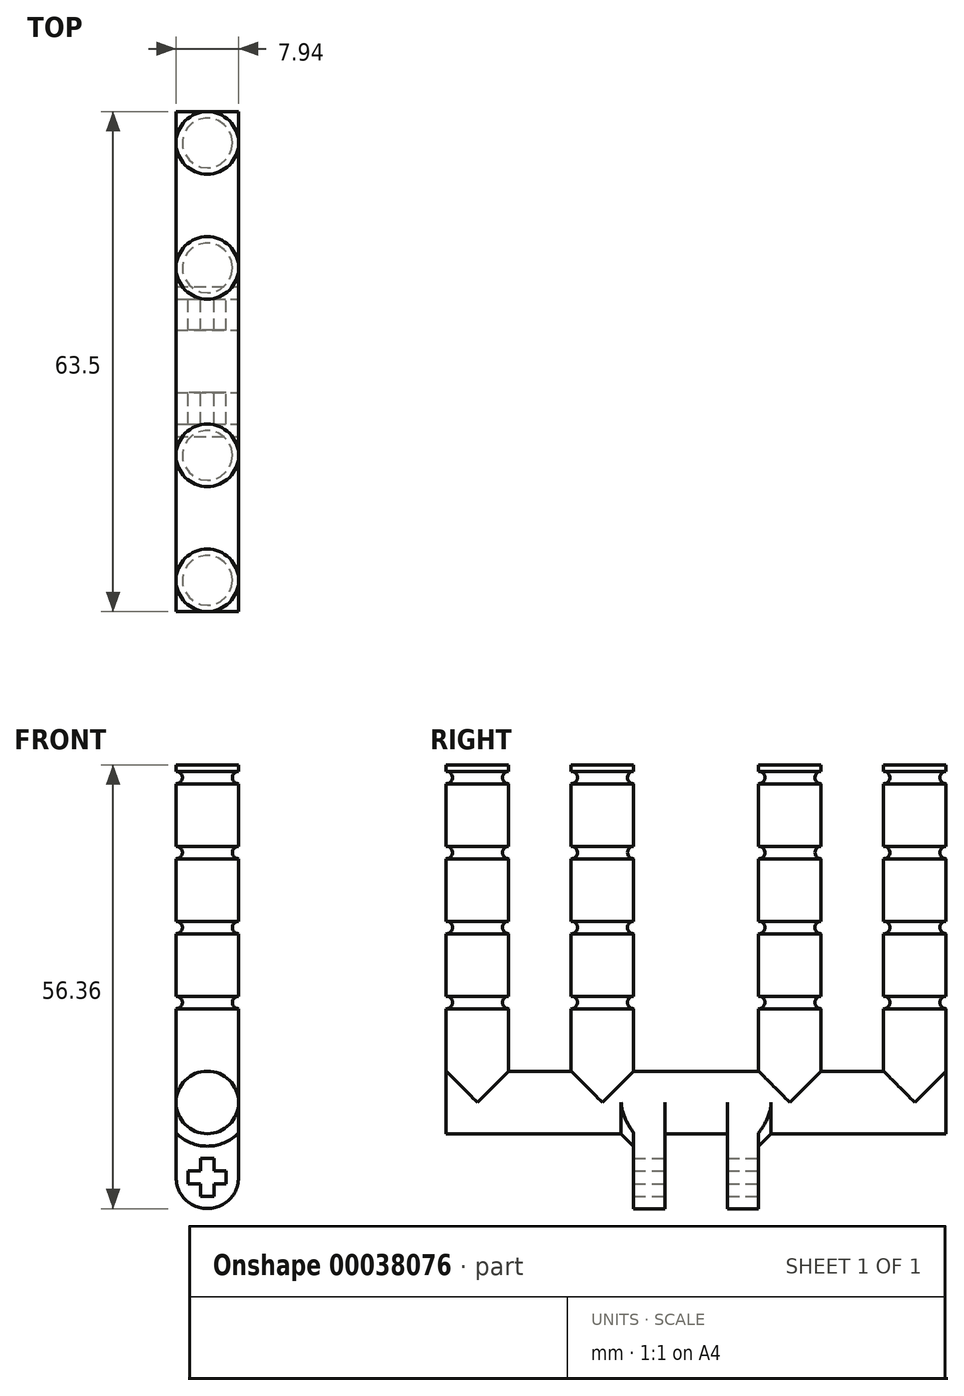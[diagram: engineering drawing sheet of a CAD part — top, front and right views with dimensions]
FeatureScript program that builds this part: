
annotation { "Feature Type Name" : "Feature", "Feature Type Description" : "" }
export const myFeature = defineFeature(function(context is Context, id is Id, definition is map)
    precondition{}
    {
        {
            var Q0;
            Q0=qCreatedBy(makeId("Top.planeOp"),FACE);
            var sketch = newSketch(context, id + "F0", { "sketchPlane" : qUnion([Q0])});
            skLineSegment(sketch, "E0.rect.bottom", {"start": v(3.97, -31.75) * mm, "end": v(-3.97, -31.75) * mm});
            skLineSegment(sketch, "E0.rect.top", {"start": v(3.97, 31.75) * mm, "end": v(-3.97, 31.75) * mm});
            skLineSegment(sketch, "E0.rect.left", {"start": v(3.97, -31.75) * mm, "end": v(3.97, 31.75) * mm});
            skLineSegment(sketch, "E0.rect.right", {"start": v(-3.97, -31.75) * mm, "end": v(-3.97, 31.75) * mm});
            skPoint(sketch, "E0.rect.middle", {"position": v(0, 0) * mm});
            skSolve(sketch);
        }
        {
            var Q0;
            Q0=qSketchRegion(id+"F0",true);
            extrude(context, id + "F1", {"entities" : qUnion([Q0]), "depth" : 7.94 * mm});
        }
        {
            var Q0;
            Q0=makeQuery(id+"F1.opExtrude","CAP_FACE",FACE,{"disambiguationData":[OSD([sQuery(id+"F0.wireOp",EDGE,"E0.rect.bottom"),sQuery(id+"F0.wireOp",EDGE,"E0.rect.top"),sQuery(id+"F0.wireOp",EDGE,"E0.rect.left"),sQuery(id+"F0.wireOp",EDGE,"E0.rect.right")])],"isStart":false});
            var sketch = newSketch(context, id + "F2", { "sketchPlane" : qUnion([Q0])});
            skLineSegment(sketch, "E1", {"start": v(0, 31.75) * mm, "end": v(0, 27.78) * mm, "construction": true});
            skLineSegment(sketch, "E2", {"start": v(0, 27.78) * mm, "end": v(0, 11.9) * mm, "construction": true});
            skLineSegment(sketch, "E3", {"start": v(0, -11.9) * mm, "end": v(0, -27.78) * mm, "construction": true});
            skLineSegment(sketch, "E4", {"start": v(0, -27.78) * mm, "end": v(0, -31.75) * mm, "construction": true});
            skCircle(sketch, "E5", {"center": v(0, 27.78) * mm, "radius": 3.97 * mm});
            skCircle(sketch, "E6", {"center": v(0, -27.78) * mm, "radius": 3.97 * mm});
            skCircle(sketch, "E7", {"center": v(0, -11.9) * mm, "radius": 3.97 * mm});
            skCircle(sketch, "E8", {"center": v(0, 11.9) * mm, "radius": 3.97 * mm});
            skSolve(sketch);
        }
        {
            var Q0;
            Q0=qSketchRegion(id+"F2",true);
            extrude(context, id + "F3", {"entities" : qUnion([Q0]), "operationType" : NewBodyOperationType.ADD, "depth" : 152.4 * mm});
        }
        {
            var Q0;
            Q0=makeQuery(id+"F1.opExtrude","CAP_FACE",FACE,{"disambiguationData":[OSD([sQuery(id+"F0.wireOp",EDGE,"E0.rect.bottom"),sQuery(id+"F0.wireOp",EDGE,"E0.rect.top"),sQuery(id+"F0.wireOp",EDGE,"E0.rect.left"),sQuery(id+"F0.wireOp",EDGE,"E0.rect.right")])],"isStart":true});
            var sketch = newSketch(context, id + "F4", { "sketchPlane" : qUnion([Q0])});
            skLineSegment(sketch, "E9", {"start": v(3.97, 0) * mm, "end": v(0, 0) * mm, "construction": true});
            skLineSegment(sketch, "E10", {"start": v(0, -3.97) * mm, "end": v(0, 3.97) * mm, "construction": true});
            skLineSegment(sketch, "E11.bottom", {"start": v(-3.97, 3.97) * mm, "end": v(3.97, 3.97) * mm});
            skLineSegment(sketch, "E11.top", {"start": v(-3.97, 7.94) * mm, "end": v(3.97, 7.94) * mm});
            skLineSegment(sketch, "E11.left", {"start": v(-3.97, 3.97) * mm, "end": v(-3.97, 7.94) * mm});
            skLineSegment(sketch, "E11.right", {"start": v(3.97, 3.97) * mm, "end": v(3.97, 7.94) * mm});
            skLineSegment(sketch, "E12.bottom", {"start": v(-3.97, -7.94) * mm, "end": v(3.97, -7.94) * mm});
            skLineSegment(sketch, "E12.top", {"start": v(-3.97, -3.97) * mm, "end": v(3.97, -3.97) * mm});
            skLineSegment(sketch, "E12.left", {"start": v(-3.97, -7.94) * mm, "end": v(-3.97, -3.97) * mm});
            skLineSegment(sketch, "E12.right", {"start": v(3.97, -7.94) * mm, "end": v(3.97, -3.97) * mm});
            skSolve(sketch);
        }
        {
            var Q0;
            Q0=qSketchRegion(id+"F4",true);
            extrude(context, id + "F5", {"entities" : qUnion([Q0]), "operationType" : NewBodyOperationType.ADD, "depth" : 9.52 * mm});
        }
        {
            var Q0;
            Q0=qCreatedBy(makeId("Right.planeOp"),FACE);
            var sketch = newSketch(context, id + "F6", { "sketchPlane" : qUnion([Q0])});
            skLineSegment(sketch, "E13", {"start": v(31.75, 7.94) * mm, "end": v(31.75, 15.88) * mm});
            skLineSegment(sketch, "E14.bottom", {"start": v(31.75, 15.88) * mm, "end": v(30.96, 15.88) * mm});
            skLineSegment(sketch, "E14.top", {"start": v(31.75, 17.46) * mm, "end": v(30.96, 17.46) * mm});
            skLineSegment(sketch, "E14.left", {"start": v(31.75, 15.88) * mm, "end": v(31.75, 17.46) * mm});
            skLineSegment(sketch, "E14.right", {"start": v(30.96, 15.88) * mm, "end": v(30.96, 17.46) * mm, "construction": true});
            skLineSegment(sketch, "E15", {"start": v(31.75, 17.46) * mm, "end": v(31.75, 25.4) * mm, "construction": true});
            skLineSegment(sketch, "E16.bottom", {"start": v(31.75, 25.4) * mm, "end": v(30.96, 25.4) * mm});
            skLineSegment(sketch, "E16.top", {"start": v(31.75, 26.99) * mm, "end": v(30.96, 26.99) * mm});
            skLineSegment(sketch, "E16.left", {"start": v(31.75, 25.4) * mm, "end": v(31.75, 26.99) * mm});
            skLineSegment(sketch, "E16.right", {"start": v(30.96, 25.4) * mm, "end": v(30.96, 26.99) * mm, "construction": true});
            skLineSegment(sketch, "E17.bottom", {"start": v(31.75, 46.04) * mm, "end": v(30.96, 46.04) * mm});
            skLineSegment(sketch, "E17.top", {"start": v(31.75, 44.45) * mm, "end": v(30.96, 44.45) * mm});
            skLineSegment(sketch, "E17.left", {"start": v(31.75, 44.45) * mm, "end": v(31.75, 46.04) * mm});
            skLineSegment(sketch, "E17.right", {"start": v(30.96, 44.45) * mm, "end": v(30.96, 46.04) * mm, "construction": true});
            skLineSegment(sketch, "E18.bottom", {"start": v(31.75, 34.92) * mm, "end": v(30.96, 34.92) * mm});
            skLineSegment(sketch, "E18.top", {"start": v(31.75, 36.51) * mm, "end": v(30.96, 36.51) * mm});
            skLineSegment(sketch, "E18.left", {"start": v(31.75, 34.92) * mm, "end": v(31.75, 36.51) * mm});
            skLineSegment(sketch, "E18.right", {"start": v(30.96, 34.92) * mm, "end": v(30.96, 36.51) * mm, "construction": true});
            skLineSegment(sketch, "E19", {"start": v(31.75, 26.99) * mm, "end": v(31.75, 34.92) * mm, "construction": true});
            skLineSegment(sketch, "E20", {"start": v(31.75, 36.51) * mm, "end": v(31.75, 44.45) * mm, "construction": true});
            skArc(sketch, "E21", {"start": v(31.75, 17.46) * mm, "mid": v(30.96, 16.67) * mm, "end": v(31.75, 15.88) * mm});
            skArc(sketch, "E22", {"start": v(31.75, 26.99) * mm, "mid": v(30.96, 26.2) * mm, "end": v(31.75, 25.4) * mm});
            skArc(sketch, "E23", {"start": v(31.75, 36.51) * mm, "mid": v(30.96, 35.72) * mm, "end": v(31.75, 34.92) * mm});
            skArc(sketch, "E24", {"start": v(31.75, 46.04) * mm, "mid": v(30.96, 45.24) * mm, "end": v(31.75, 44.45) * mm});
            skLineSegment(sketch, "E25", {"start": v(31.75, 46.04) * mm, "end": v(31.75, 46.83) * mm});
            skLineSegment(sketch, "E26.bottom", {"start": v(31.75, 46.83) * mm, "end": v(27.78, 46.83) * mm});
            skLineSegment(sketch, "E26.top", {"start": v(31.75, 160.34) * mm, "end": v(27.78, 160.34) * mm});
            skLineSegment(sketch, "E26.left", {"start": v(31.75, 46.83) * mm, "end": v(31.75, 160.34) * mm});
            skLineSegment(sketch, "E26.right", {"start": v(27.78, 46.83) * mm, "end": v(27.78, 160.34) * mm});
            skSolve(sketch);
        }
        {
            var Q0;
            Q0=qSketchRegion(id+"F6",true);
            var Q1;
            Q1=makeQuery(id+"F3.opExtrude","CAP_EDGE",EDGE,{"disambiguationData":[OSD([sQuery(id+"F2.wireOp",EDGE,"E5")])],"isStart":false});
            revolve(context, id + "F7", {"operationType" : NewBodyOperationType.REMOVE, "entities" : qUnion([Q0]), "axis" : qUnion([Q1]), "revolveType" : RevolveType.FULL, "oppositeDirection" : true});
        }
        {
            var Q0;
            Q0=qCreatedBy(makeId("Right.planeOp"),FACE);
            var sketch = newSketch(context, id + "F8", { "sketchPlane" : qUnion([Q0])});
            skLineSegment(sketch, "E27", {"start": v(15.87, 7.94) * mm, "end": v(11.9, 7.94) * mm, "construction": true});
            skLineSegment(sketch, "E28", {"start": v(15.87, 7.94) * mm, "end": v(15.87, 15.88) * mm, "construction": true});
            skLineSegment(sketch, "E29.bottom", {"start": v(15.87, 15.88) * mm, "end": v(15.08, 15.88) * mm, "construction": true});
            skLineSegment(sketch, "E29.top", {"start": v(15.87, 17.46) * mm, "end": v(15.08, 17.46) * mm, "construction": true});
            skLineSegment(sketch, "E29.left", {"start": v(15.87, 15.88) * mm, "end": v(15.87, 17.46) * mm});
            skLineSegment(sketch, "E29.right", {"start": v(15.08, 15.88) * mm, "end": v(15.08, 17.46) * mm, "construction": true});
            skLineSegment(sketch, "E30", {"start": v(15.87, 17.46) * mm, "end": v(15.87, 25.4) * mm, "construction": true});
            skLineSegment(sketch, "E31.bottom", {"start": v(15.87, 25.4) * mm, "end": v(15.08, 25.4) * mm, "construction": true});
            skLineSegment(sketch, "E31.top", {"start": v(15.88, 26.99) * mm, "end": v(15.08, 26.99) * mm, "construction": true});
            skLineSegment(sketch, "E31.left", {"start": v(15.87, 25.4) * mm, "end": v(15.87, 26.99) * mm});
            skLineSegment(sketch, "E31.right", {"start": v(15.08, 25.4) * mm, "end": v(15.08, 26.99) * mm, "construction": true});
            skArc(sketch, "E32", {"start": v(15.88, 26.99) * mm, "mid": v(15.08, 26.2) * mm, "end": v(15.87, 25.4) * mm});
            skArc(sketch, "E33", {"start": v(15.87, 17.46) * mm, "mid": v(15.08, 16.67) * mm, "end": v(15.87, 15.88) * mm});
            skLineSegment(sketch, "E34", {"start": v(15.88, 26.99) * mm, "end": v(15.88, 34.93) * mm, "construction": true});
            skLineSegment(sketch, "E35", {"start": v(15.87, 36.51) * mm, "end": v(15.87, 44.45) * mm, "construction": true});
            skLineSegment(sketch, "E36.bottom", {"start": v(15.88, 34.93) * mm, "end": v(15.08, 34.93) * mm, "construction": true});
            skLineSegment(sketch, "E36.top", {"start": v(15.87, 36.51) * mm, "end": v(15.08, 36.51) * mm, "construction": true});
            skLineSegment(sketch, "E36.left", {"start": v(15.88, 34.93) * mm, "end": v(15.88, 36.51) * mm});
            skLineSegment(sketch, "E36.right", {"start": v(15.08, 34.93) * mm, "end": v(15.08, 36.51) * mm, "construction": true});
            skLineSegment(sketch, "E37.bottom", {"start": v(15.87, 44.45) * mm, "end": v(15.08, 44.45) * mm, "construction": true});
            skLineSegment(sketch, "E37.top", {"start": v(15.88, 46.04) * mm, "end": v(15.08, 46.04) * mm, "construction": true});
            skLineSegment(sketch, "E37.left", {"start": v(15.87, 44.45) * mm, "end": v(15.87, 46.04) * mm});
            skLineSegment(sketch, "E37.right", {"start": v(15.08, 44.45) * mm, "end": v(15.08, 46.04) * mm, "construction": true});
            skLineSegment(sketch, "E38", {"start": v(15.88, 46.04) * mm, "end": v(15.88, 46.83) * mm});
            skLineSegment(sketch, "E39.bottom", {"start": v(15.88, 46.83) * mm, "end": v(11.9, 46.83) * mm});
            skLineSegment(sketch, "E39.top", {"start": v(15.87, 160.34) * mm, "end": v(11.9, 160.34) * mm});
            skLineSegment(sketch, "E39.left", {"start": v(15.88, 46.83) * mm, "end": v(15.87, 160.34) * mm});
            skLineSegment(sketch, "E39.right", {"start": v(11.9, 46.83) * mm, "end": v(11.9, 160.34) * mm});
            skArc(sketch, "E40", {"start": v(15.88, 46.04) * mm, "mid": v(15.08, 45.24) * mm, "end": v(15.87, 44.45) * mm});
            skArc(sketch, "E41", {"start": v(15.87, 36.51) * mm, "mid": v(15.08, 35.72) * mm, "end": v(15.88, 34.93) * mm});
            skSolve(sketch);
        }
        {
            var Q0;
            Q0=qSketchRegion(id+"F8",true);
            var Q1;
            Q1=makeQuery(id+"F3.opExtrude","CAP_EDGE",EDGE,{"disambiguationData":[OSD([sQuery(id+"F2.wireOp",EDGE,"E8")])],"isStart":false});
            revolve(context, id + "F9", {"operationType" : NewBodyOperationType.REMOVE, "entities" : qUnion([Q0]), "axis" : qUnion([Q1]), "revolveType" : RevolveType.FULL, "oppositeDirection" : true});
        }
        {
            var Q0;
            Q0=qCreatedBy(makeId("Right.planeOp"),FACE);
            var sketch = newSketch(context, id + "F10", { "sketchPlane" : qUnion([Q0])});
            skLineSegment(sketch, "E42", {"start": v(-11.9, 7.94) * mm, "end": v(-7.94, 7.94) * mm});
            skLineSegment(sketch, "E43", {"start": v(-7.94, 7.94) * mm, "end": v(-7.94, 15.88) * mm, "construction": true});
            skLineSegment(sketch, "E44.bottom", {"start": v(-7.94, 15.88) * mm, "end": v(-8.73, 15.88) * mm});
            skLineSegment(sketch, "E44.top", {"start": v(-7.94, 17.46) * mm, "end": v(-8.73, 17.46) * mm});
            skLineSegment(sketch, "E44.left", {"start": v(-7.94, 15.88) * mm, "end": v(-7.94, 17.46) * mm});
            skLineSegment(sketch, "E44.right", {"start": v(-8.73, 15.88) * mm, "end": v(-8.73, 17.46) * mm, "construction": true});
            skLineSegment(sketch, "E45", {"start": v(-7.94, 17.46) * mm, "end": v(-7.94, 25.4) * mm, "construction": true});
            skLineSegment(sketch, "E46.bottom", {"start": v(-7.94, 25.4) * mm, "end": v(-8.73, 25.4) * mm});
            skLineSegment(sketch, "E46.top", {"start": v(-7.94, 26.99) * mm, "end": v(-8.73, 26.99) * mm});
            skLineSegment(sketch, "E46.left", {"start": v(-7.94, 25.4) * mm, "end": v(-7.94, 26.99) * mm});
            skLineSegment(sketch, "E46.right", {"start": v(-8.73, 25.4) * mm, "end": v(-8.73, 26.99) * mm, "construction": true});
            skLineSegment(sketch, "E47", {"start": v(-7.94, 26.99) * mm, "end": v(-7.94, 34.92) * mm, "construction": true});
            skLineSegment(sketch, "E48.bottom", {"start": v(-7.94, 34.92) * mm, "end": v(-8.73, 34.92) * mm});
            skLineSegment(sketch, "E48.top", {"start": v(-7.94, 36.51) * mm, "end": v(-8.73, 36.51) * mm, "construction": true});
            skLineSegment(sketch, "E48.left", {"start": v(-7.94, 34.92) * mm, "end": v(-7.94, 36.51) * mm});
            skLineSegment(sketch, "E48.right", {"start": v(-8.73, 34.92) * mm, "end": v(-8.73, 36.51) * mm, "construction": true});
            skLineSegment(sketch, "E49", {"start": v(-7.94, 36.51) * mm, "end": v(-7.94, 44.45) * mm, "construction": true});
            skLineSegment(sketch, "E50.bottom", {"start": v(-7.94, 44.45) * mm, "end": v(-8.73, 44.45) * mm});
            skLineSegment(sketch, "E50.top", {"start": v(-7.94, 46.04) * mm, "end": v(-8.73, 46.04) * mm, "construction": true});
            skLineSegment(sketch, "E50.left", {"start": v(-7.94, 44.45) * mm, "end": v(-7.94, 46.04) * mm});
            skLineSegment(sketch, "E50.right", {"start": v(-8.73, 44.45) * mm, "end": v(-8.73, 46.04) * mm, "construction": true});
            skLineSegment(sketch, "E51", {"start": v(-7.94, 46.04) * mm, "end": v(-7.94, 46.83) * mm, "construction": true});
            skLineSegment(sketch, "E52.bottom", {"start": v(-7.94, 46.83) * mm, "end": v(-11.9, 46.83) * mm});
            skLineSegment(sketch, "E52.top", {"start": v(-7.94, 160.34) * mm, "end": v(-11.9, 160.34) * mm});
            skLineSegment(sketch, "E52.left", {"start": v(-7.94, 46.83) * mm, "end": v(-7.94, 160.34) * mm});
            skLineSegment(sketch, "E52.right", {"start": v(-11.9, 46.83) * mm, "end": v(-11.9, 160.34) * mm});
            skArc(sketch, "E53", {"start": v(-7.94, 46.04) * mm, "mid": v(-8.73, 45.24) * mm, "end": v(-7.94, 44.45) * mm});
            skArc(sketch, "E54", {"start": v(-7.94, 36.51) * mm, "mid": v(-8.73, 35.72) * mm, "end": v(-7.94, 34.92) * mm});
            skArc(sketch, "E55", {"start": v(-7.94, 26.99) * mm, "mid": v(-8.73, 26.2) * mm, "end": v(-7.94, 25.4) * mm});
            skArc(sketch, "E56", {"start": v(-7.94, 17.46) * mm, "mid": v(-8.73, 16.67) * mm, "end": v(-7.94, 15.88) * mm});
            skSolve(sketch);
        }
        {
            var Q0;
            Q0=qSketchRegion(id+"F10",true);
            var Q1;
            Q1=makeQuery(id+"F3.opExtrude","CAP_EDGE",EDGE,{"disambiguationData":[OSD([sQuery(id+"F2.wireOp",EDGE,"E7")])],"isStart":false});
            revolve(context, id + "F11", {"operationType" : NewBodyOperationType.REMOVE, "entities" : qUnion([Q0]), "axis" : qUnion([Q1]), "revolveType" : RevolveType.FULL, "oppositeDirection" : true});
        }
        {
            var Q0;
            Q0=qCreatedBy(makeId("Right.planeOp"),FACE);
            var sketch = newSketch(context, id + "F12", { "sketchPlane" : qUnion([Q0])});
            skLineSegment(sketch, "E57", {"start": v(-27.78, 7.94) * mm, "end": v(-23.81, 7.94) * mm});
            skLineSegment(sketch, "E58", {"start": v(-23.81, 7.94) * mm, "end": v(-23.81, 15.88) * mm, "construction": true});
            skLineSegment(sketch, "E59.bottom", {"start": v(-23.81, 15.88) * mm, "end": v(-24.6, 15.88) * mm});
            skLineSegment(sketch, "E59.top", {"start": v(-23.81, 17.46) * mm, "end": v(-24.6, 17.46) * mm, "construction": true});
            skLineSegment(sketch, "E59.left", {"start": v(-23.81, 15.88) * mm, "end": v(-23.81, 17.46) * mm});
            skLineSegment(sketch, "E59.right", {"start": v(-24.6, 15.88) * mm, "end": v(-24.6, 17.46) * mm, "construction": true});
            skLineSegment(sketch, "E60", {"start": v(-23.81, 17.46) * mm, "end": v(-23.81, 25.4) * mm, "construction": true});
            skLineSegment(sketch, "E61.bottom", {"start": v(-23.81, 25.4) * mm, "end": v(-24.6, 25.4) * mm});
            skLineSegment(sketch, "E61.top", {"start": v(-23.81, 26.99) * mm, "end": v(-24.6, 26.99) * mm, "construction": true});
            skLineSegment(sketch, "E61.left", {"start": v(-23.81, 25.4) * mm, "end": v(-23.81, 26.99) * mm});
            skLineSegment(sketch, "E61.right", {"start": v(-24.6, 25.4) * mm, "end": v(-24.6, 26.99) * mm, "construction": true});
            skLineSegment(sketch, "E62", {"start": v(-23.81, 26.99) * mm, "end": v(-23.81, 34.92) * mm, "construction": true});
            skLineSegment(sketch, "E63.bottom", {"start": v(-23.81, 34.92) * mm, "end": v(-24.6, 34.92) * mm});
            skLineSegment(sketch, "E63.top", {"start": v(-23.81, 36.51) * mm, "end": v(-24.6, 36.51) * mm, "construction": true});
            skLineSegment(sketch, "E63.left", {"start": v(-23.81, 34.92) * mm, "end": v(-23.81, 36.51) * mm});
            skLineSegment(sketch, "E63.right", {"start": v(-24.6, 34.92) * mm, "end": v(-24.6, 36.51) * mm, "construction": true});
            skLineSegment(sketch, "E64", {"start": v(-23.81, 36.51) * mm, "end": v(-23.81, 44.45) * mm, "construction": true});
            skLineSegment(sketch, "E65.bottom", {"start": v(-23.81, 44.45) * mm, "end": v(-24.6, 44.45) * mm, "construction": true});
            skLineSegment(sketch, "E65.top", {"start": v(-23.81, 46.04) * mm, "end": v(-24.6, 46.04) * mm});
            skLineSegment(sketch, "E65.left", {"start": v(-23.81, 44.45) * mm, "end": v(-23.81, 46.04) * mm});
            skLineSegment(sketch, "E65.right", {"start": v(-24.6, 44.45) * mm, "end": v(-24.6, 46.04) * mm, "construction": true});
            skArc(sketch, "E66", {"start": v(-23.81, 46.04) * mm, "mid": v(-24.6, 45.24) * mm, "end": v(-23.81, 44.45) * mm});
            skArc(sketch, "E67", {"start": v(-23.81, 36.51) * mm, "mid": v(-24.6, 35.72) * mm, "end": v(-23.81, 34.92) * mm});
            skArc(sketch, "E68", {"start": v(-23.81, 26.99) * mm, "mid": v(-24.6, 26.2) * mm, "end": v(-23.81, 25.4) * mm});
            skArc(sketch, "E69", {"start": v(-23.81, 17.46) * mm, "mid": v(-24.6, 16.67) * mm, "end": v(-23.81, 15.88) * mm});
            skLineSegment(sketch, "E70", {"start": v(-23.81, 46.04) * mm, "end": v(-23.81, 46.83) * mm, "construction": true});
            skLineSegment(sketch, "E71.bottom", {"start": v(-23.81, 46.83) * mm, "end": v(-27.78, 46.83) * mm});
            skLineSegment(sketch, "E71.top", {"start": v(-23.81, 160.34) * mm, "end": v(-27.78, 160.34) * mm});
            skLineSegment(sketch, "E71.left", {"start": v(-23.81, 46.83) * mm, "end": v(-23.81, 160.34) * mm});
            skLineSegment(sketch, "E71.right", {"start": v(-27.78, 46.83) * mm, "end": v(-27.78, 160.34) * mm});
            skSolve(sketch);
        }
        {
            var Q0;
            Q0=qSketchRegion(id+"F12",true);
            var Q1;
            Q1=makeQuery(id+"F3.opExtrude","CAP_EDGE",EDGE,{"disambiguationData":[OSD([sQuery(id+"F2.wireOp",EDGE,"E6")])],"isStart":false});
            revolve(context, id + "F13", {"operationType" : NewBodyOperationType.REMOVE, "entities" : qUnion([Q0]), "axis" : qUnion([Q1]), "revolveType" : RevolveType.FULL, "oppositeDirection" : true});
        }
        {
            var Q0;
            {var subQ0=sQuery(id+"F0.wireOp",EDGE,"E0.rect.right");Q0=makeQuery(id+"F3.boolean.opBoolean","SPLIT",EDGE,{"disambiguationData":[TD([makeQuery(id+"F1.opExtrude","CAP_FACE",FACE,{"disambiguationData":[OSD([sQuery(id+"F0.wireOp",EDGE,"E0.rect.bottom"),sQuery(id+"F0.wireOp",EDGE,"E0.rect.top"),sQuery(id+"F0.wireOp",EDGE,"E0.rect.left"),subQ0])],"isStart":false}),makeQuery(id+"F1.opExtrude","SWEPT_FACE",FACE,{"disambiguationData":[OSD([subQ0])]}),makeQuery(id+"F3.opExtrude","SWEPT_FACE",FACE,{"disambiguationData":[OSD([sQuery(id+"F2.wireOp",EDGE,"E5")])]}),makeQuery(id+"F3.opExtrude","SWEPT_FACE",FACE,{"disambiguationData":[OSD([sQuery(id+"F2.wireOp",EDGE,"E8")])]})])],"derivedFrom":makeQuery(id+"F1.opExtrude","CAP_EDGE",EDGE,{"disambiguationData":[OSD([subQ0])],"isStart":false})});}
            var Q1;
            {var subQ0=sQuery(id+"F0.wireOp",EDGE,"E0.rect.right");Q1=makeQuery(id+"F3.boolean.opBoolean","SPLIT",EDGE,{"disambiguationData":[TD([makeQuery(id+"F1.opExtrude","CAP_FACE",FACE,{"disambiguationData":[OSD([sQuery(id+"F0.wireOp",EDGE,"E0.rect.bottom"),sQuery(id+"F0.wireOp",EDGE,"E0.rect.top"),sQuery(id+"F0.wireOp",EDGE,"E0.rect.left"),subQ0])],"isStart":false}),makeQuery(id+"F1.opExtrude","SWEPT_FACE",FACE,{"disambiguationData":[OSD([subQ0])]}),makeQuery(id+"F3.opExtrude","SWEPT_FACE",FACE,{"disambiguationData":[OSD([sQuery(id+"F2.wireOp",EDGE,"E7")])]}),makeQuery(id+"F3.opExtrude","SWEPT_FACE",FACE,{"disambiguationData":[OSD([sQuery(id+"F2.wireOp",EDGE,"E8")])]})])],"derivedFrom":makeQuery(id+"F1.opExtrude","CAP_EDGE",EDGE,{"disambiguationData":[OSD([subQ0])],"isStart":false})});}
            var Q2;
            {var subQ0=sQuery(id+"F0.wireOp",EDGE,"E0.rect.right");Q2=makeQuery(id+"F3.boolean.opBoolean","SPLIT",EDGE,{"disambiguationData":[TD([makeQuery(id+"F1.opExtrude","CAP_FACE",FACE,{"disambiguationData":[OSD([sQuery(id+"F0.wireOp",EDGE,"E0.rect.bottom"),sQuery(id+"F0.wireOp",EDGE,"E0.rect.top"),sQuery(id+"F0.wireOp",EDGE,"E0.rect.left"),subQ0])],"isStart":false}),makeQuery(id+"F1.opExtrude","SWEPT_FACE",FACE,{"disambiguationData":[OSD([subQ0])]}),makeQuery(id+"F3.opExtrude","SWEPT_FACE",FACE,{"disambiguationData":[OSD([sQuery(id+"F2.wireOp",EDGE,"E6")])]}),makeQuery(id+"F3.opExtrude","SWEPT_FACE",FACE,{"disambiguationData":[OSD([sQuery(id+"F2.wireOp",EDGE,"E7")])]})])],"derivedFrom":makeQuery(id+"F1.opExtrude","CAP_EDGE",EDGE,{"disambiguationData":[OSD([subQ0])],"isStart":false})});}
            var Q3;
            {var subQ0=sQuery(id+"F0.wireOp",EDGE,"E0.rect.right");var subQ1=sQuery(id+"F0.wireOp",EDGE,"E0.rect.top");Q3=makeQuery(id+"F3.boolean.opBoolean","SPLIT",EDGE,{"disambiguationData":[TD([makeQuery(id+"F1.opExtrude","CAP_FACE",FACE,{"disambiguationData":[OSD([sQuery(id+"F0.wireOp",EDGE,"E0.rect.bottom"),subQ1,sQuery(id+"F0.wireOp",EDGE,"E0.rect.left"),subQ0])],"isStart":false}),makeQuery(id+"F1.opExtrude","SWEPT_FACE",FACE,{"disambiguationData":[OSD([subQ1])]}),makeQuery(id+"F1.opExtrude","SWEPT_FACE",FACE,{"disambiguationData":[OSD([subQ0])]}),makeQuery(id+"F3.opExtrude","SWEPT_FACE",FACE,{"disambiguationData":[OSD([sQuery(id+"F2.wireOp",EDGE,"E5")])]})])],"derivedFrom":makeQuery(id+"F1.opExtrude","CAP_EDGE",EDGE,{"disambiguationData":[OSD([subQ0])],"isStart":false})});}
            var Q4;
            {var subQ0=sQuery(id+"F0.wireOp",EDGE,"E0.rect.bottom");var subQ1=sQuery(id+"F0.wireOp",EDGE,"E0.rect.right");Q4=makeQuery(id+"F3.boolean.opBoolean","SPLIT",EDGE,{"disambiguationData":[TD([makeQuery(id+"F1.opExtrude","SWEPT_FACE",FACE,{"disambiguationData":[OSD([subQ0])]}),makeQuery(id+"F1.opExtrude","CAP_FACE",FACE,{"disambiguationData":[OSD([subQ0,sQuery(id+"F0.wireOp",EDGE,"E0.rect.top"),sQuery(id+"F0.wireOp",EDGE,"E0.rect.left"),subQ1])],"isStart":false}),makeQuery(id+"F1.opExtrude","SWEPT_FACE",FACE,{"disambiguationData":[OSD([subQ1])]}),makeQuery(id+"F3.opExtrude","SWEPT_FACE",FACE,{"disambiguationData":[OSD([sQuery(id+"F2.wireOp",EDGE,"E6")])]})])],"derivedFrom":makeQuery(id+"F1.opExtrude","CAP_EDGE",EDGE,{"disambiguationData":[OSD([subQ1])],"isStart":false})});}
            var Q5;
            {var subQ0=sQuery(id+"F0.wireOp",EDGE,"E0.rect.right");var subQ1=sQuery(id+"F0.wireOp",EDGE,"E0.rect.bottom");Q5=makeQuery(id+"F5.boolean.opBoolean","SPLIT",EDGE,{"disambiguationData":[TD([makeQuery(id+"F1.opExtrude","SWEPT_FACE",FACE,{"disambiguationData":[OSD([subQ1])]})])],"derivedFrom":makeQuery(id+"F1.opExtrude","CAP_EDGE",EDGE,{"disambiguationData":[OSD([subQ0])],"isStart":true})});}
            var Q6;
            {var subQ0=sQuery(id+"F0.wireOp",EDGE,"E0.rect.right");Q6=makeQuery(id+"F5.boolean.opBoolean","SPLIT",EDGE,{"disambiguationData":[TD([makeQuery(id+"F5.opExtrude","SWEPT_FACE",FACE,{"disambiguationData":[OSD([sQuery(id+"F4.wireOp",EDGE,"E11.bottom")])]})])],"derivedFrom":makeQuery(id+"F1.opExtrude","CAP_EDGE",EDGE,{"disambiguationData":[OSD([subQ0])],"isStart":true})});}
            var Q7;
            {var subQ0=sQuery(id+"F0.wireOp",EDGE,"E0.rect.right");var subQ1=sQuery(id+"F0.wireOp",EDGE,"E0.rect.top");Q7=makeQuery(id+"F5.boolean.opBoolean","SPLIT",EDGE,{"disambiguationData":[TD([makeQuery(id+"F1.opExtrude","SWEPT_FACE",FACE,{"disambiguationData":[OSD([subQ1])]})])],"derivedFrom":makeQuery(id+"F1.opExtrude","CAP_EDGE",EDGE,{"disambiguationData":[OSD([subQ0])],"isStart":true})});}
            var Q8;
            {var subQ0=sQuery(id+"F0.wireOp",EDGE,"E0.rect.left");Q8=makeQuery(id+"F3.boolean.opBoolean","SPLIT",EDGE,{"disambiguationData":[TD([makeQuery(id+"F1.opExtrude","CAP_FACE",FACE,{"disambiguationData":[OSD([sQuery(id+"F0.wireOp",EDGE,"E0.rect.bottom"),sQuery(id+"F0.wireOp",EDGE,"E0.rect.top"),subQ0,sQuery(id+"F0.wireOp",EDGE,"E0.rect.right")])],"isStart":false}),makeQuery(id+"F1.opExtrude","SWEPT_FACE",FACE,{"disambiguationData":[OSD([subQ0])]}),makeQuery(id+"F3.opExtrude","SWEPT_FACE",FACE,{"disambiguationData":[OSD([sQuery(id+"F2.wireOp",EDGE,"E5")])]}),makeQuery(id+"F3.opExtrude","SWEPT_FACE",FACE,{"disambiguationData":[OSD([sQuery(id+"F2.wireOp",EDGE,"E8")])]})])],"derivedFrom":makeQuery(id+"F1.opExtrude","CAP_EDGE",EDGE,{"disambiguationData":[OSD([subQ0])],"isStart":false})});}
            var Q9;
            {var subQ0=sQuery(id+"F0.wireOp",EDGE,"E0.rect.left");var subQ1=sQuery(id+"F0.wireOp",EDGE,"E0.rect.top");Q9=makeQuery(id+"F3.boolean.opBoolean","SPLIT",EDGE,{"disambiguationData":[TD([makeQuery(id+"F1.opExtrude","CAP_FACE",FACE,{"disambiguationData":[OSD([sQuery(id+"F0.wireOp",EDGE,"E0.rect.bottom"),subQ1,subQ0,sQuery(id+"F0.wireOp",EDGE,"E0.rect.right")])],"isStart":false}),makeQuery(id+"F1.opExtrude","SWEPT_FACE",FACE,{"disambiguationData":[OSD([subQ1])]}),makeQuery(id+"F1.opExtrude","SWEPT_FACE",FACE,{"disambiguationData":[OSD([subQ0])]}),makeQuery(id+"F3.opExtrude","SWEPT_FACE",FACE,{"disambiguationData":[OSD([sQuery(id+"F2.wireOp",EDGE,"E5")])]})])],"derivedFrom":makeQuery(id+"F1.opExtrude","CAP_EDGE",EDGE,{"disambiguationData":[OSD([subQ0])],"isStart":false})});}
            var Q10;
            {var subQ0=sQuery(id+"F0.wireOp",EDGE,"E0.rect.left");Q10=makeQuery(id+"F5.boolean.opBoolean","SPLIT",EDGE,{"disambiguationData":[TD([makeQuery(id+"F5.opExtrude","SWEPT_FACE",FACE,{"disambiguationData":[OSD([sQuery(id+"F4.wireOp",EDGE,"E11.bottom")])]})])],"derivedFrom":makeQuery(id+"F1.opExtrude","CAP_EDGE",EDGE,{"disambiguationData":[OSD([subQ0])],"isStart":true})});}
            var Q11;
            {var subQ0=sQuery(id+"F0.wireOp",EDGE,"E0.rect.left");var subQ1=sQuery(id+"F0.wireOp",EDGE,"E0.rect.top");Q11=makeQuery(id+"F5.boolean.opBoolean","SPLIT",EDGE,{"disambiguationData":[TD([makeQuery(id+"F1.opExtrude","SWEPT_FACE",FACE,{"disambiguationData":[OSD([subQ1])]})])],"derivedFrom":makeQuery(id+"F1.opExtrude","CAP_EDGE",EDGE,{"disambiguationData":[OSD([subQ0])],"isStart":true})});}
            var Q12;
            {var subQ0=sQuery(id+"F0.wireOp",EDGE,"E0.rect.left");Q12=makeQuery(id+"F3.boolean.opBoolean","SPLIT",EDGE,{"disambiguationData":[TD([makeQuery(id+"F1.opExtrude","CAP_FACE",FACE,{"disambiguationData":[OSD([sQuery(id+"F0.wireOp",EDGE,"E0.rect.bottom"),sQuery(id+"F0.wireOp",EDGE,"E0.rect.top"),subQ0,sQuery(id+"F0.wireOp",EDGE,"E0.rect.right")])],"isStart":false}),makeQuery(id+"F1.opExtrude","SWEPT_FACE",FACE,{"disambiguationData":[OSD([subQ0])]}),makeQuery(id+"F3.opExtrude","SWEPT_FACE",FACE,{"disambiguationData":[OSD([sQuery(id+"F2.wireOp",EDGE,"E7")])]}),makeQuery(id+"F3.opExtrude","SWEPT_FACE",FACE,{"disambiguationData":[OSD([sQuery(id+"F2.wireOp",EDGE,"E8")])]})])],"derivedFrom":makeQuery(id+"F1.opExtrude","CAP_EDGE",EDGE,{"disambiguationData":[OSD([subQ0])],"isStart":false})});}
            var Q13;
            {var subQ0=sQuery(id+"F0.wireOp",EDGE,"E0.rect.left");Q13=makeQuery(id+"F3.boolean.opBoolean","SPLIT",EDGE,{"disambiguationData":[TD([makeQuery(id+"F1.opExtrude","CAP_FACE",FACE,{"disambiguationData":[OSD([sQuery(id+"F0.wireOp",EDGE,"E0.rect.bottom"),sQuery(id+"F0.wireOp",EDGE,"E0.rect.top"),subQ0,sQuery(id+"F0.wireOp",EDGE,"E0.rect.right")])],"isStart":false}),makeQuery(id+"F1.opExtrude","SWEPT_FACE",FACE,{"disambiguationData":[OSD([subQ0])]}),makeQuery(id+"F3.opExtrude","SWEPT_FACE",FACE,{"disambiguationData":[OSD([sQuery(id+"F2.wireOp",EDGE,"E6")])]}),makeQuery(id+"F3.opExtrude","SWEPT_FACE",FACE,{"disambiguationData":[OSD([sQuery(id+"F2.wireOp",EDGE,"E7")])]})])],"derivedFrom":makeQuery(id+"F1.opExtrude","CAP_EDGE",EDGE,{"disambiguationData":[OSD([subQ0])],"isStart":false})});}
            var Q14;
            {var subQ0=sQuery(id+"F0.wireOp",EDGE,"E0.rect.left");var subQ1=sQuery(id+"F0.wireOp",EDGE,"E0.rect.bottom");Q14=makeQuery(id+"F5.boolean.opBoolean","SPLIT",EDGE,{"disambiguationData":[TD([makeQuery(id+"F1.opExtrude","SWEPT_FACE",FACE,{"disambiguationData":[OSD([subQ1])]})])],"derivedFrom":makeQuery(id+"F1.opExtrude","CAP_EDGE",EDGE,{"disambiguationData":[OSD([subQ0])],"isStart":true})});}
            var Q15;
            Q15=makeQuery(id+"F5.opExtrude","CAP_EDGE",EDGE,{"disambiguationData":[OSD([sQuery(id+"F4.wireOp",EDGE,"E11.right")])],"isStart":false});
            var Q16;
            Q16=makeQuery(id+"F5.opExtrude","CAP_EDGE",EDGE,{"disambiguationData":[OSD([sQuery(id+"F4.wireOp",EDGE,"E11.left")])],"isStart":false});
            var Q17;
            Q17=makeQuery(id+"F5.opExtrude","CAP_EDGE",EDGE,{"disambiguationData":[OSD([sQuery(id+"F4.wireOp",EDGE,"E12.left")])],"isStart":false});
            var Q18;
            Q18=makeQuery(id+"F5.opExtrude","CAP_EDGE",EDGE,{"disambiguationData":[OSD([sQuery(id+"F4.wireOp",EDGE,"E12.right")])],"isStart":false});
            fillet(context, id + "F14", {"entities" : qUnion([Q0, Q1, Q2, Q3, Q4, Q5, Q6, Q7, Q8, Q9, Q10, Q11, Q12, Q13, Q14, Q15, Q16, Q17, Q18]), "radius" : 3.97 * mm, "tangentPropagation" : true, "allowEdgeOverflow" : false});
        }
        {
            var Q0;
            {var subQ0=makeQuery(id+"F5.opExtrude","SWEPT_FACE",FACE,{"disambiguationData":[OSD([sQuery(id+"F4.wireOp",EDGE,"E12.bottom")])]});var subQ1=sQuery(id+"F0.wireOp",EDGE,"E0.rect.left");var subQ2=sQuery(id+"F0.wireOp",EDGE,"E0.rect.top");Q0=makeQuery(id+"F14.opFillet","BLEND_EDGE",EDGE,{"blendedFrom":[makeQuery(id+"F5.boolean.opBoolean","SPLIT",EDGE,{"disambiguationData":[TD([makeQuery(id+"F1.opExtrude","SWEPT_FACE",FACE,{"disambiguationData":[OSD([subQ2])]})])],"derivedFrom":makeQuery(id+"F1.opExtrude","CAP_EDGE",EDGE,{"disambiguationData":[OSD([subQ1])],"isStart":true})}),subQ0],"blendedInto":[subQ0]});}
            var Q1;
            {var subQ0=makeQuery(id+"F5.opExtrude","SWEPT_FACE",FACE,{"disambiguationData":[OSD([sQuery(id+"F4.wireOp",EDGE,"E11.top")])]});var subQ1=sQuery(id+"F0.wireOp",EDGE,"E0.rect.left");var subQ2=sQuery(id+"F0.wireOp",EDGE,"E0.rect.bottom");Q1=makeQuery(id+"F14.opFillet","BLEND_EDGE",EDGE,{"blendedFrom":[makeQuery(id+"F5.boolean.opBoolean","SPLIT",EDGE,{"disambiguationData":[TD([makeQuery(id+"F1.opExtrude","SWEPT_FACE",FACE,{"disambiguationData":[OSD([subQ2])]})])],"derivedFrom":makeQuery(id+"F1.opExtrude","CAP_EDGE",EDGE,{"disambiguationData":[OSD([subQ1])],"isStart":true})}),subQ0],"blendedInto":[subQ0]});}
            chamfer(context, id + "F15", {"entities" : qUnion([Q0, Q1]), "width" : 1.59 * mm, "tangentPropagation" : true});
        }
        {
            var Q0;
            Q0=makeQuery(id+"F5.opExtrude","SWEPT_FACE",FACE,{"disambiguationData":[OSD([sQuery(id+"F4.wireOp",EDGE,"E12.bottom")])]});
            var sketch = newSketch(context, id + "F16", { "sketchPlane" : qUnion([Q0])});
            skLineSegment(sketch, "E72.rect.bottom", {"start": v(2.41, -6.4) * mm, "end": v(-2.41, -6.4) * mm});
            skLineSegment(sketch, "E72.rect.top", {"start": v(2.41, -4.71) * mm, "end": v(-2.41, -4.71) * mm});
            skLineSegment(sketch, "E72.rect.left", {"start": v(2.41, -6.4) * mm, "end": v(2.41, -4.71) * mm});
            skLineSegment(sketch, "E72.rect.right", {"start": v(-2.41, -6.4) * mm, "end": v(-2.41, -4.71) * mm});
            skPoint(sketch, "E72.rect.middle", {"position": v(0, -5.56) * mm});
            skLineSegment(sketch, "E73.rect.bottom", {"start": v(0.84, -7.97) * mm, "end": v(-0.84, -7.97) * mm});
            skLineSegment(sketch, "E73.rect.top", {"start": v(0.84, -3.14) * mm, "end": v(-0.84, -3.14) * mm});
            skLineSegment(sketch, "E73.rect.left", {"start": v(0.84, -7.97) * mm, "end": v(0.84, -3.14) * mm});
            skLineSegment(sketch, "E73.rect.right", {"start": v(-0.84, -7.97) * mm, "end": v(-0.84, -3.14) * mm});
            skSolve(sketch);
        }
        {
            var Q0;
            Q0=qSketchRegion(id+"F16",true);
            var Q1;
            Q1=makeQuery(id+"F5.opExtrude","SWEPT_FACE",FACE,{"disambiguationData":[OSD([sQuery(id+"F4.wireOp",EDGE,"E11.top")])]});
            extrude(context, id + "F17", {"entities" : qUnion([Q0]), "operationType" : NewBodyOperationType.REMOVE, "endBound" : BoundingType.UP_TO_SURFACE, "oppositeDirection" : true, "endBoundEntityFace" : qUnion([Q1]), "depth" : 25.4 * mm});
        }
    });
